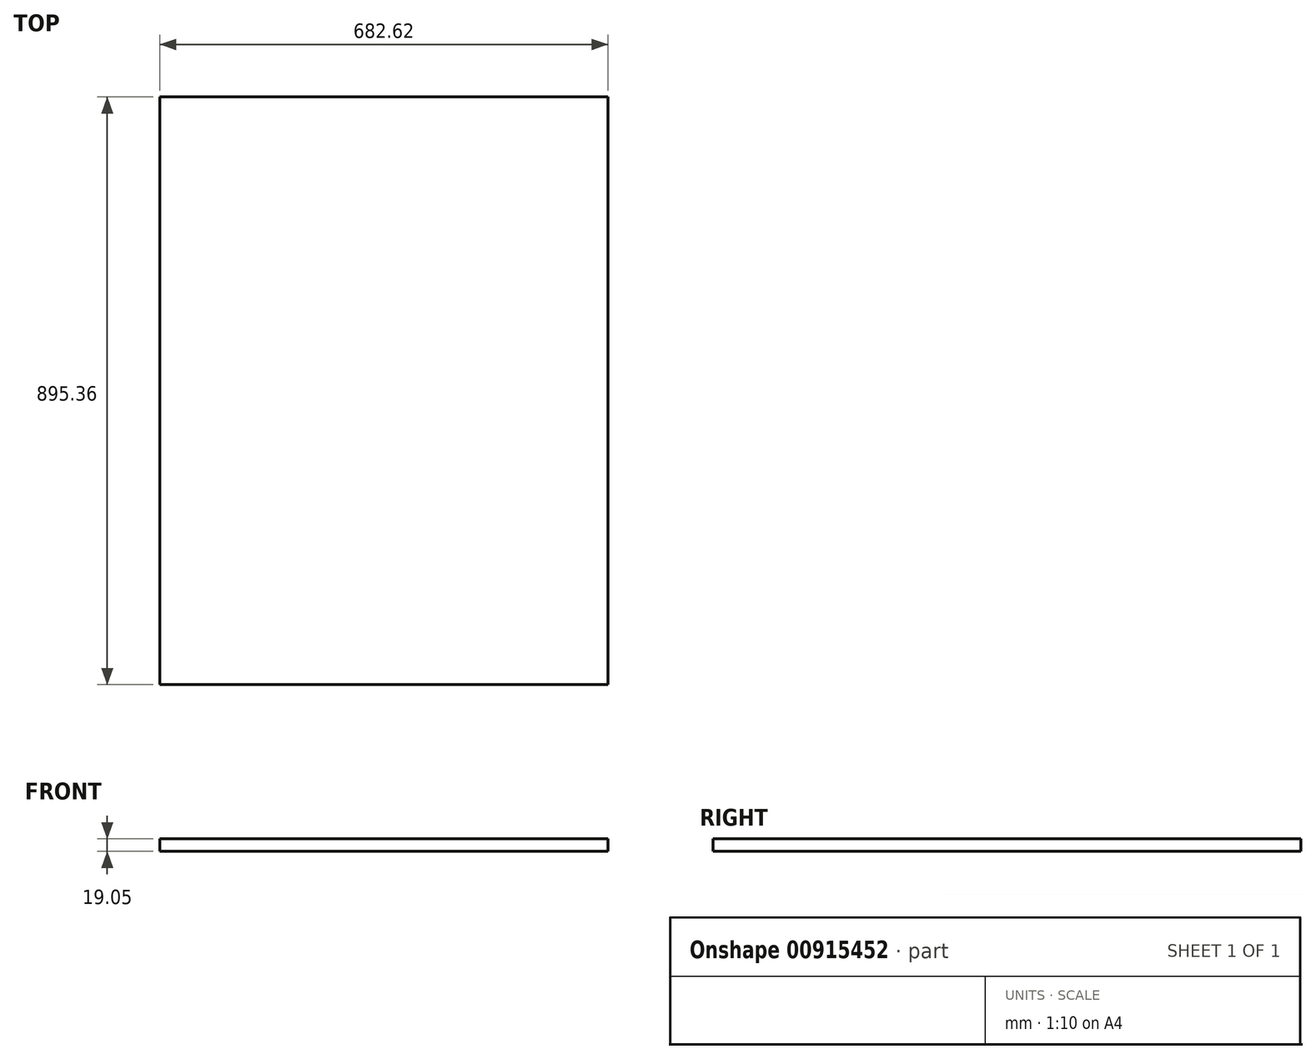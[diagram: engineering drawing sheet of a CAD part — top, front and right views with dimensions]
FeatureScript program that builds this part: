
annotation { "Feature Type Name" : "Feature", "Feature Type Description" : "" }
export const myFeature = defineFeature(function(context is Context, id is Id, definition is map)
    precondition{}
    {
        {
            var Q0;
            Q0=qCreatedBy(makeId("Top.planeOp"),FACE);
            var sketch = newSketch(context, id + "F0", { "sketchPlane" : qUnion([Q0])});
            skLineSegment(sketch, "E0.bottom", {"start": v(341.31, 447.68) * mm, "end": v(-341.31, 447.68) * mm});
            skLineSegment(sketch, "E0.top", {"start": v(341.31, -447.68) * mm, "end": v(-341.31, -447.68) * mm});
            skLineSegment(sketch, "E0.left", {"start": v(341.31, 447.68) * mm, "end": v(341.31, -447.68) * mm});
            skLineSegment(sketch, "E0.right", {"start": v(-341.31, 447.68) * mm, "end": v(-341.31, -447.68) * mm});
            skPoint(sketch, "E0.middle", {"position": v(0, 0) * mm});
            skSolve(sketch);
        }
        {
            var Q0;
            Q0=makeQuery(id+"F0.imprint","IMPRINT",FACE,{"disambiguationData":[TD([[makeQuery(id+"F0.imprint","IMPRINT",EDGE,{"derivedFrom":sQuery(id+"F0.wireOp",EDGE,"E0.bottom")}),1.0]])]});
            extrude(context, id + "F1", {"entities" : qUnion([Q0]), "depth" : 19.05 * mm, "offsetDistance" : 25.4 * mm});
        }
    });
